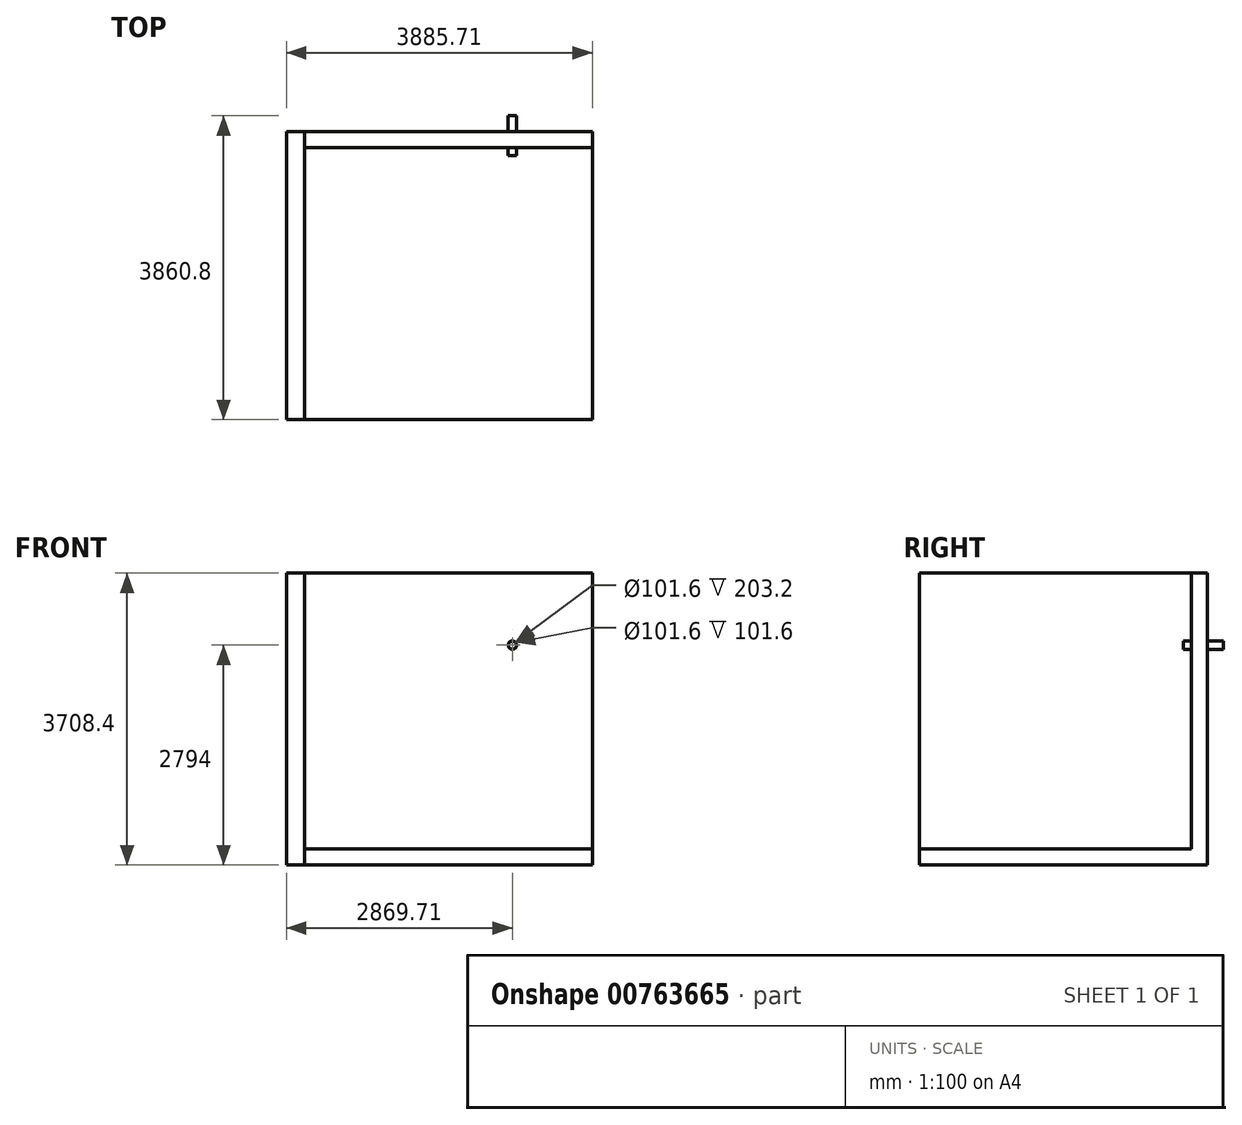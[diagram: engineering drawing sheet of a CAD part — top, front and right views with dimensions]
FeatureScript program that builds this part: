
annotation { "Feature Type Name" : "Feature", "Feature Type Description" : "" }
export const myFeature = defineFeature(function(context is Context, id is Id, definition is map)
    precondition{}
    {
        {
            var Q0;
            Q0=qCreatedBy(makeId("Front.planeOp"),FACE);
            var sketch = newSketch(context, id + "F0", { "sketchPlane" : qUnion([Q0])});
            skLineSegment(sketch, "E0.bottom", {"start": v(-1828.8, 1854.2) * mm, "end": v(1828.8, 1854.2) * mm});
            skLineSegment(sketch, "E0.top", {"start": v(-1828.8, -1854.2) * mm, "end": v(1828.8, -1854.2) * mm});
            skLineSegment(sketch, "E0.left", {"start": v(-1828.8, 1854.2) * mm, "end": v(-1828.8, -1854.2) * mm});
            skLineSegment(sketch, "E0.right", {"start": v(1828.8, 1854.2) * mm, "end": v(1828.8, -1854.2) * mm});
            skPoint(sketch, "E0.middle", {"position": v(0, 0) * mm});
            skLineSegment(sketch, "E1.top", {"start": v(-1828.8, -1651) * mm, "end": v(1828.8, -1651) * mm});
            skLineSegment(sketch, "E1.left", {"start": v(-1828.8, -1854.2) * mm, "end": v(-1828.8, -1651) * mm});
            skLineSegment(sketch, "E1.right", {"start": v(1828.8, -1854.2) * mm, "end": v(1828.8, -1651) * mm});
            skSolve(sketch);
        }
        {
            var Q0;
            {var subQ0=sQuery(id+"F0.wireOp",EDGE,"E0.bottom");Q0=makeQuery(id+"F0.imprint","IMPRINT",FACE,{"disambiguationData":[TD([[makeQuery(id+"F0.imprint","IMPRINT",EDGE,{"derivedFrom":subQ0}),-1.0]])]});}
            extrude(context, id + "F1", {"entities" : qUnion([Q0]), "depth" : 203.2 * mm, "offsetDistance" : 25.4 * mm});
        }
        {
            var Q0;
            {var subQ0=sQuery(id+"F0.wireOp",EDGE,"E0.top");Q0=makeQuery(id+"F0.imprint","IMPRINT",FACE,{"disambiguationData":[TD([[makeQuery(id+"F0.imprint","IMPRINT",EDGE,{"derivedFrom":subQ0}),1.0]])]});}
            extrude(context, id + "F2", {"entities" : qUnion([Q0]), "operationType" : NewBodyOperationType.ADD, "depth" : 3657.6 * mm, "offsetDistance" : 25.4 * mm});
        }
        {
            var Q0;
            {var subQ0=sQuery(id+"F0.wireOp",EDGE,"E1.top");var subQ1=sQuery(id+"F0.wireOp",EDGE,"E0.right");var subQ2=sQuery(id+"F0.wireOp",EDGE,"E0.left");Q0=makeQuery(id+"F2.boolean.opBoolean","MERGE",FACE,{"derivedFrom":[makeQuery(id+"F1.opExtrude","CAP_FACE",FACE,{"disambiguationData":[OSD([sQuery(id+"F0.wireOp",EDGE,"E0.bottom"),subQ2,subQ1,subQ0])],"isStart":true}),makeQuery(id+"F2.opExtrude","CAP_FACE",FACE,{"disambiguationData":[OSD([sQuery(id+"F0.wireOp",EDGE,"E0.top"),subQ2,subQ1,subQ0])],"isStart":true})]});}
            var sketch = newSketch(context, id + "F3", { "sketchPlane" : qUnion([Q0])});
            skLineSegment(sketch, "E2.bottom", {"start": v(-1828.8, -1854.2) * mm, "end": v(-2056.91, -1854.2) * mm});
            skLineSegment(sketch, "E2.top", {"start": v(-1828.8, 1854.2) * mm, "end": v(-2056.91, 1854.2) * mm});
            skLineSegment(sketch, "E2.left", {"start": v(-1828.8, -1854.2) * mm, "end": v(-1828.8, 1854.2) * mm});
            skLineSegment(sketch, "E2.right", {"start": v(-2056.91, -1854.2) * mm, "end": v(-2056.91, 1854.2) * mm});
            skLineSegment(sketch, "E3", {"start": v(0, 0) * mm, "end": v(0, 2419.12) * mm, "construction": true});
            skLineSegment(sketch, "E4.MirrorCS", {"start": v(1828.8, 1854.2) * mm, "end": v(2056.91, 1854.2) * mm});
            skLineSegment(sketch, "E5.MirrorCS", {"start": v(2056.91, -1854.2) * mm, "end": v(2056.91, 1854.2) * mm});
            skLineSegment(sketch, "E6.MirrorCS", {"start": v(1828.8, -1854.2) * mm, "end": v(2056.91, -1854.2) * mm});
            skLineSegment(sketch, "E7.MirrorCS", {"start": v(1828.8, -1854.2) * mm, "end": v(1828.8, 1854.2) * mm});
            skSolve(sketch);
        }
        {
            var Q0;
            Q0=makeQuery(id+"F3.imprint","IMPRINT",FACE,{"disambiguationData":[TD([[makeQuery(id+"F3.imprint","IMPRINT",EDGE,{"derivedFrom":sQuery(id+"F3.wireOp",EDGE,"E4.MirrorCS")}),-1.0]])]});
            extrude(context, id + "F4", {"entities" : qUnion([Q0]), "oppositeDirection" : true, "depth" : 3657.6 * mm, "offsetDistance" : 25.4 * mm});
        }
        {
            var Q0;
            Q0=makeQuery(id+"F1.opExtrude","CAP_FACE",FACE,{"disambiguationData":[OSD([sQuery(id+"F0.wireOp",EDGE,"E0.bottom"),sQuery(id+"F0.wireOp",EDGE,"E0.left"),sQuery(id+"F0.wireOp",EDGE,"E0.right"),sQuery(id+"F0.wireOp",EDGE,"E1.top")])],"isStart":false});
            var sketch = newSketch(context, id + "F5", { "sketchPlane" : qUnion([Q0])});
            skCircle(sketch, "E8", {"center": v(812.8, 939.8) * mm, "radius": 53.34 * mm});
            skCircle(sketch, "E9", {"center": v(812.8, 939.8) * mm, "radius": 50.8 * mm});
            skSolve(sketch);
        }
        {
            var Q0;
            Q0 = qSketchRegion(id + "F5", true);
            extrude(context, id + "F6", {"entities" : qUnion([Q0]), "depth" : 101.6 * mm, "offsetDistance" : 25.4 * mm});
        }
        {
            var Q0;
            Q0 = qSketchRegion(id + "F5", true);
            extrude(context, id + "F7", {"entities" : qUnion([Q0]), "operationType" : NewBodyOperationType.ADD, "oppositeDirection" : true, "depth" : 406.4 * mm, "offsetDistance" : 25.4 * mm});
        }
        {
            var Q0;
            Q0=makeQuery(id+"F4.opExtrude","SWEPT_FACE",FACE,{"disambiguationData":[OSD([sQuery(id+"F3.wireOp",EDGE,"E7.MirrorCS")])]});
            cPlane(context, id + "F8", {"entities" : qUnion([Q0]), "cplaneType" : CPlaneType.OFFSET, "offset" : 2641.6 * mm, "width" : 152.4 * mm, "height" : 152.4 * mm});
        }
    });
